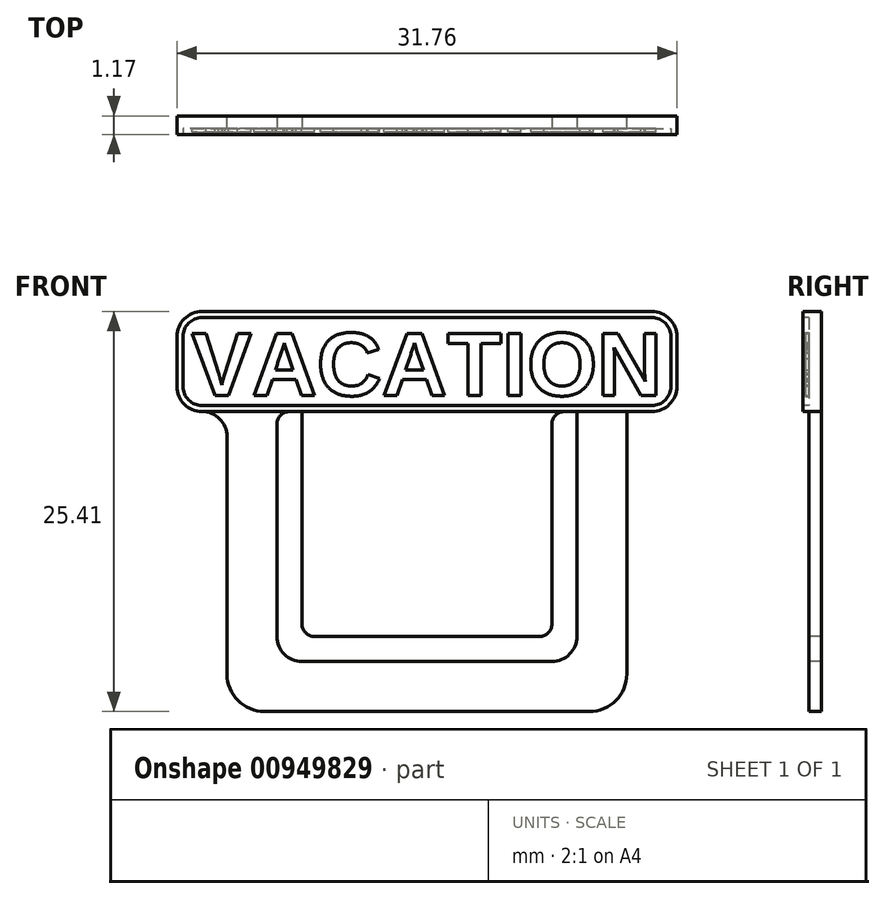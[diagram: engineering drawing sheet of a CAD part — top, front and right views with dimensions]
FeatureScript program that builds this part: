
annotation { "Feature Type Name" : "Feature", "Feature Type Description" : "" }
export const myFeature = defineFeature(function(context is Context, id is Id, definition is map)
    precondition{}
    {
        {
            var Q0;
            Q0=qCreatedBy(makeId("Front.planeOp"),FACE);
            var sketch = newSketch(context, id + "F0", { "sketchPlane" : qUnion([Q0])});
            skLineSegment(sketch, "E0.bottom", {"start": v(12.7, 9.53) * mm, "end": v(-12.7, 9.53) * mm});
            skLineSegment(sketch, "E0.top", {"start": v(12.7, -9.53) * mm, "end": v(-12.7, -9.53) * mm});
            skLineSegment(sketch, "E0.left", {"start": v(12.7, 9.53) * mm, "end": v(12.7, -9.53) * mm});
            skLineSegment(sketch, "E0.right", {"start": v(-12.7, 9.53) * mm, "end": v(-12.7, -9.53) * mm});
            skPoint(sketch, "E0.middle", {"position": v(0, 0) * mm});
            skSolve(sketch);
        }
        {
            var Q0;
            Q0=makeQuery(id+"F0.imprint","IMPRINT",FACE,{"disambiguationData":[TD([[makeQuery(id+"F0.imprint","IMPRINT",EDGE,{"derivedFrom":sQuery(id+"F0.wireOp",EDGE,"E0.bottom")}),1.0]])]});
            extrude(context, id + "F1", {"entities" : qUnion([Q0]), "depth" : 0.8 * mm, "offsetDistance" : 25.4 * mm});
        }
        {
            var Q0;
            Q0=makeQuery(id+"F1.opExtrude","SWEPT_EDGE",EDGE,{"disambiguationData":[OSD([sQuery(id+"F0.wireOp",EDGE,"E0.top"),sQuery(id+"F0.wireOp",EDGE,"E0.left")])]});
            var Q1;
            Q1=makeQuery(id+"F1.opExtrude","SWEPT_EDGE",EDGE,{"disambiguationData":[OSD([sQuery(id+"F0.wireOp",EDGE,"E0.top"),sQuery(id+"F0.wireOp",EDGE,"E0.right")])]});
            fillet(context, id + "F2", {"entities" : qUnion([Q0, Q1]), "radius" : 2.38 * mm, "tangentPropagation" : true, "allowEdgeOverflow" : false});
        }
        {
            var Q0;
            Q0=makeQuery(id+"F1.opExtrude","CAP_FACE",FACE,{"disambiguationData":[OSD([sQuery(id+"F0.wireOp",EDGE,"E0.bottom"),sQuery(id+"F0.wireOp",EDGE,"E0.top"),sQuery(id+"F0.wireOp",EDGE,"E0.left"),sQuery(id+"F0.wireOp",EDGE,"E0.right")])],"isStart":false});
            var sketch = newSketch(context, id + "F3", { "sketchPlane" : qUnion([Q0])});
            skLineSegment(sketch, "E1.bottom", {"start": v(9.52, 9.53) * mm, "end": v(-9.53, 9.53) * mm});
            skLineSegment(sketch, "E1.top", {"start": v(9.53, -6.35) * mm, "end": v(-9.53, -6.35) * mm});
            skLineSegment(sketch, "E1.left", {"start": v(9.52, 9.53) * mm, "end": v(9.53, -6.35) * mm});
            skLineSegment(sketch, "E1.right", {"start": v(-9.53, 9.53) * mm, "end": v(-9.52, -6.35) * mm});
            skPoint(sketch, "E1.middle", {"position": v(0, 0) * mm});
            skSolve(sketch);
        }
        {
            var Q0;
            Q0=makeQuery(id+"F3.imprint","IMPRINT",FACE,{"disambiguationData":[TD([[makeQuery(id+"F3.imprint","IMPRINT",EDGE,{"derivedFrom":sQuery(id+"F3.wireOp",EDGE,"E1.bottom")}),1.0]])]});
            extrude(context, id + "F4", {"entities" : qUnion([Q0]), "operationType" : NewBodyOperationType.REMOVE, "oppositeDirection" : true, "depth" : 4.93 * mm, "offsetDistance" : 25.4 * mm});
        }
        {
            var Q0;
            Q0=makeQuery(id+"F1.opExtrude","CAP_FACE",FACE,{"disambiguationData":[OSD([sQuery(id+"F0.wireOp",EDGE,"E0.bottom"),sQuery(id+"F0.wireOp",EDGE,"E0.top"),sQuery(id+"F0.wireOp",EDGE,"E0.left"),sQuery(id+"F0.wireOp",EDGE,"E0.right")])],"isStart":false});
            var sketch = newSketch(context, id + "F5", { "sketchPlane" : qUnion([Q0])});
            skLineSegment(sketch, "E2.bottom", {"start": v(-15.88, 9.53) * mm, "end": v(15.87, 9.53) * mm});
            skLineSegment(sketch, "E2.top", {"start": v(-15.88, 15.88) * mm, "end": v(15.87, 15.88) * mm});
            skLineSegment(sketch, "E2.left", {"start": v(-15.88, 9.53) * mm, "end": v(-15.88, 15.88) * mm});
            skLineSegment(sketch, "E2.right", {"start": v(15.87, 9.53) * mm, "end": v(15.87, 15.88) * mm});
            skSolve(sketch);
        }
        {
            var Q0;
            Q0=makeQuery(id+"F5.imprint","IMPRINT",FACE,{"disambiguationData":[TD([[makeQuery(id+"F5.imprint","IMPRINT",EDGE,{"derivedFrom":sQuery(id+"F5.wireOp",EDGE,"E2.top")}),-1.0]])]});
            extrude(context, id + "F6", {"entities" : qUnion([Q0]), "operationType" : NewBodyOperationType.ADD, "oppositeDirection" : true, "depth" : 0.8 * mm, "offsetDistance" : 25.4 * mm});
        }
        {
            var Q0;
            Q0=makeQuery(id+"F6.opExtrude","SWEPT_EDGE",EDGE,{"disambiguationData":[OSD([sQuery(id+"F5.wireOp",EDGE,"E2.top"),sQuery(id+"F5.wireOp",EDGE,"E2.left")])]});
            var Q1;
            Q1=makeQuery(id+"F6.opExtrude","SWEPT_EDGE",EDGE,{"disambiguationData":[OSD([sQuery(id+"F5.wireOp",EDGE,"E2.top"),sQuery(id+"F5.wireOp",EDGE,"E2.right")])]});
            var Q2;
            Q2=makeQuery(id+"F6.opExtrude","SWEPT_EDGE",EDGE,{"disambiguationData":[OSD([sQuery(id+"F5.wireOp",EDGE,"E2.bottom"),sQuery(id+"F5.wireOp",EDGE,"E2.right")])]});
            var Q3;
            Q3=makeQuery(id+"F1.opExtrude","SWEPT_EDGE",EDGE,{"disambiguationData":[OSD([sQuery(id+"F0.wireOp",EDGE,"E0.bottom"),sQuery(id+"F0.wireOp",EDGE,"E0.left")])]});
            var Q4;
            Q4=makeQuery(id+"F6.opExtrude","SWEPT_EDGE",EDGE,{"disambiguationData":[OSD([sQuery(id+"F5.wireOp",EDGE,"E2.bottom"),sQuery(id+"F5.wireOp",EDGE,"E2.left")])]});
            var Q5;
            Q5=makeQuery(id+"F1.opExtrude","SWEPT_EDGE",EDGE,{"disambiguationData":[OSD([sQuery(id+"F0.wireOp",EDGE,"E0.bottom"),sQuery(id+"F0.wireOp",EDGE,"E0.right")])]});
            fillet(context, id + "F7", {"entities" : qUnion([Q0, Q1, Q2, Q3, Q4, Q5]), "radius" : 1.59 * mm, "tangentPropagation" : true, "allowEdgeOverflow" : false});
        }
        {
            var Q0;
            Q0=makeQuery(id+"F4.boolean.opBoolean","COPY",EDGE,{"derivedFrom":makeQuery(id+"F4.opExtrude","SWEPT_EDGE",EDGE,{"disambiguationData":[OSD([sQuery(id+"F3.wireOp",EDGE,"E1.top"),sQuery(id+"F3.wireOp",EDGE,"E1.right")])]})});
            var Q1;
            Q1=makeQuery(id+"F4.boolean.opBoolean","COPY",EDGE,{"derivedFrom":makeQuery(id+"F4.opExtrude","SWEPT_EDGE",EDGE,{"disambiguationData":[OSD([sQuery(id+"F3.wireOp",EDGE,"E1.top"),sQuery(id+"F3.wireOp",EDGE,"E1.left")])]})});
            fillet(context, id + "F8", {"entities" : qUnion([Q0, Q1]), "radius" : 1.59 * mm, "tangentPropagation" : true, "allowEdgeOverflow" : false});
        }
        {
            var Q0;
            Q0=makeQuery(id+"F6.boolean.opBoolean","MERGE",FACE,{"derivedFrom":[makeQuery(id+"F1.opExtrude","CAP_FACE",FACE,{"disambiguationData":[OSD([sQuery(id+"F0.wireOp",EDGE,"E0.bottom"),sQuery(id+"F0.wireOp",EDGE,"E0.top"),sQuery(id+"F0.wireOp",EDGE,"E0.left"),sQuery(id+"F0.wireOp",EDGE,"E0.right")])],"isStart":false}),makeQuery(id+"F6.opExtrude","CAP_FACE",FACE,{"disambiguationData":[OSD([sQuery(id+"F5.wireOp",EDGE,"E2.bottom"),sQuery(id+"F5.wireOp",EDGE,"E2.top"),sQuery(id+"F5.wireOp",EDGE,"E2.left"),sQuery(id+"F5.wireOp",EDGE,"E2.right")])],"isStart":true})]});
            var sketch = newSketch(context, id + "F9", { "sketchPlane" : qUnion([Q0])});
            skLineSegment(sketch, "E3.bottom", {"start": v(-7.94, 9.53) * mm, "end": v(7.94, 9.53) * mm});
            skLineSegment(sketch, "E3.top", {"start": v(-7.94, -4.76) * mm, "end": v(7.94, -4.76) * mm});
            skLineSegment(sketch, "E3.left", {"start": v(-7.94, 9.53) * mm, "end": v(-7.94, -4.76) * mm});
            skLineSegment(sketch, "E3.right", {"start": v(7.94, 9.53) * mm, "end": v(7.94, -4.76) * mm});
            skSolve(sketch);
        }
        {
            var Q0;
            Q0=makeQuery(id+"F9.imprint","IMPRINT",FACE,{"disambiguationData":[TD([[makeQuery(id+"F9.imprint","IMPRINT",EDGE,{"derivedFrom":sQuery(id+"F9.wireOp",EDGE,"E3.bottom")}),1.0]])]});
            extrude(context, id + "F10", {"entities" : qUnion([Q0]), "operationType" : NewBodyOperationType.ADD, "oppositeDirection" : true, "depth" : 0.8 * mm, "offsetDistance" : 25.4 * mm});
        }
        {
            var Q0;
            Q0=makeQuery(id+"F10.opExtrude","SWEPT_EDGE",EDGE,{"disambiguationData":[OSD([sQuery(id+"F5.wireOp",EDGE,"E2.bottom"),sQuery(id+"F9.wireOp",EDGE,"E3.bottom"),sQuery(id+"F9.wireOp",EDGE,"E3.left")])]});
            var Q1;
            Q1=makeQuery(id+"F4.boolean.opBoolean","COPY",EDGE,{"derivedFrom":makeQuery(id+"F4.opExtrude","SWEPT_EDGE",EDGE,{"disambiguationData":[OSD([sQuery(id+"F0.wireOp",EDGE,"E0.bottom"),sQuery(id+"F3.wireOp",EDGE,"E1.bottom"),sQuery(id+"F3.wireOp",EDGE,"E1.right")])]})});
            var Q2;
            Q2=makeQuery(id+"F10.opExtrude","SWEPT_EDGE",EDGE,{"disambiguationData":[OSD([sQuery(id+"F5.wireOp",EDGE,"E2.bottom"),sQuery(id+"F9.wireOp",EDGE,"E3.bottom"),sQuery(id+"F9.wireOp",EDGE,"E3.right")])]});
            var Q3;
            Q3=makeQuery(id+"F4.boolean.opBoolean","COPY",EDGE,{"derivedFrom":makeQuery(id+"F4.opExtrude","SWEPT_EDGE",EDGE,{"disambiguationData":[OSD([sQuery(id+"F0.wireOp",EDGE,"E0.bottom"),sQuery(id+"F3.wireOp",EDGE,"E1.bottom"),sQuery(id+"F3.wireOp",EDGE,"E1.left")])]})});
            fillet(context, id + "F11", {"entities" : qUnion([Q0, Q1, Q2, Q3]), "radius" : 0.8 * mm, "tangentPropagation" : true, "allowEdgeOverflow" : false});
        }
        {
            var Q0;
            Q0=makeQuery(id+"F10.opExtrude","SWEPT_EDGE",EDGE,{"disambiguationData":[OSD([sQuery(id+"F9.wireOp",EDGE,"E3.top"),sQuery(id+"F9.wireOp",EDGE,"E3.left")])]});
            var Q1;
            Q1=makeQuery(id+"F10.opExtrude","SWEPT_EDGE",EDGE,{"disambiguationData":[OSD([sQuery(id+"F9.wireOp",EDGE,"E3.top"),sQuery(id+"F9.wireOp",EDGE,"E3.right")])]});
            fillet(context, id + "F12", {"entities" : qUnion([Q0, Q1]), "radius" : 0.8 * mm, "tangentPropagation" : true, "allowEdgeOverflow" : false});
        }
        {
            var Q0;
            Q0=makeQuery(id+"F10.boolean.opBoolean","MERGE",FACE,{"derivedFrom":[makeQuery(id+"F6.boolean.opBoolean","MERGE",FACE,{"derivedFrom":[makeQuery(id+"F1.opExtrude","CAP_FACE",FACE,{"disambiguationData":[OSD([sQuery(id+"F0.wireOp",EDGE,"E0.bottom"),sQuery(id+"F0.wireOp",EDGE,"E0.top"),sQuery(id+"F0.wireOp",EDGE,"E0.left"),sQuery(id+"F0.wireOp",EDGE,"E0.right")])],"isStart":false}),makeQuery(id+"F6.opExtrude","CAP_FACE",FACE,{"disambiguationData":[OSD([sQuery(id+"F5.wireOp",EDGE,"E2.bottom"),sQuery(id+"F5.wireOp",EDGE,"E2.top"),sQuery(id+"F5.wireOp",EDGE,"E2.left"),sQuery(id+"F5.wireOp",EDGE,"E2.right")])],"isStart":true})]}),makeQuery(id+"F10.opExtrude","CAP_FACE",FACE,{"disambiguationData":[OSD([sQuery(id+"F9.wireOp",EDGE,"E3.bottom"),sQuery(id+"F9.wireOp",EDGE,"E3.top"),sQuery(id+"F9.wireOp",EDGE,"E3.left"),sQuery(id+"F9.wireOp",EDGE,"E3.right")])],"isStart":true})]});
            var sketch = newSketch(context, id + "F13", { "sketchPlane" : qUnion([Q0])});
            skArc(sketch, "E4.0", {"start": v(-14.29, 15.88) * mm, "mid": v(-15.41, 15.41) * mm, "end": v(-15.88, 14.29) * mm});
            skLineSegment(sketch, "E5.0", {"start": v(-15.88, 11.11) * mm, "end": v(-15.88, 14.29) * mm});
            skArc(sketch, "E6.0", {"start": v(-15.88, 11.11) * mm, "mid": v(-15.41, 9.99) * mm, "end": v(-14.29, 9.53) * mm});
            skLineSegment(sketch, "E7.0", {"start": v(-14.29, 15.88) * mm, "end": v(14.29, 15.88) * mm});
            skArc(sketch, "E8.0", {"start": v(15.87, 14.29) * mm, "mid": v(15.41, 15.41) * mm, "end": v(14.29, 15.88) * mm});
            skLineSegment(sketch, "E9.0", {"start": v(15.87, 11.11) * mm, "end": v(15.87, 14.29) * mm});
            skArc(sketch, "E10.0", {"start": v(14.29, 9.53) * mm, "mid": v(15.41, 9.99) * mm, "end": v(15.87, 11.11) * mm});
            skLineSegment(sketch, "E11", {"start": v(-14.29, 9.53) * mm, "end": v(14.29, 9.53) * mm});
            skSolve(sketch);
        }
        {
            var Q0;
            Q0=makeQuery(id+"F13.imprint","IMPRINT",FACE,{"disambiguationData":[TD([[makeQuery(id+"F13.imprint","IMPRINT",EDGE,{"derivedFrom":sQuery(id+"F13.wireOp",EDGE,"E4.0")}),1.0]])]});
            extrude(context, id + "F14", {"entities" : qUnion([Q0]), "operationType" : NewBodyOperationType.ADD, "depth" : 0.38 * mm, "offsetDistance" : 25.4 * mm});
        }
        {
            var Q0;
            Q0=makeQuery(id+"F14.opExtrude","CAP_FACE",FACE,{"disambiguationData":[OSD([sQuery(id+"F13.wireOp",EDGE,"E4.0"),sQuery(id+"F13.wireOp",EDGE,"E5.0"),sQuery(id+"F13.wireOp",EDGE,"E6.0"),sQuery(id+"F13.wireOp",EDGE,"E7.0"),sQuery(id+"F13.wireOp",EDGE,"E8.0"),sQuery(id+"F13.wireOp",EDGE,"E9.0"),sQuery(id+"F13.wireOp",EDGE,"E10.0"),sQuery(id+"F13.wireOp",EDGE,"E11")])],"isStart":false});
            var sketch = newSketch(context, id + "F15", { "sketchPlane" : qUnion([Q0])});
            skArc(sketch, "E12.0", {"start": v(-14.29, 15.88) * mm, "mid": v(-15.41, 15.41) * mm, "end": v(-15.88, 14.29) * mm});
            skLineSegment(sketch, "E13.0", {"start": v(-14.29, 15.88) * mm, "end": v(14.29, 15.88) * mm});
            skLineSegment(sketch, "E14.0", {"start": v(-15.88, 11.11) * mm, "end": v(-15.88, 14.29) * mm});
            skArc(sketch, "E15.0", {"start": v(-15.88, 11.11) * mm, "mid": v(-15.41, 9.99) * mm, "end": v(-14.29, 9.53) * mm});
            skLineSegment(sketch, "E16.0", {"start": v(-14.29, 9.53) * mm, "end": v(14.29, 9.53) * mm});
            skArc(sketch, "E17.0", {"start": v(14.29, 9.53) * mm, "mid": v(15.41, 9.99) * mm, "end": v(15.87, 11.11) * mm});
            skArc(sketch, "E18.0", {"start": v(15.87, 14.29) * mm, "mid": v(15.41, 15.41) * mm, "end": v(14.29, 15.88) * mm});
            skArc(sketch, "E19", {"start": v(-14.29, 15.5) * mm, "mid": v(-15.14, 15.14) * mm, "end": v(-15.5, 14.29) * mm});
            skArc(sketch, "E20", {"start": v(-15.5, 11.11) * mm, "mid": v(-15.14, 10.26) * mm, "end": v(-14.29, 9.9) * mm});
            skArc(sketch, "E21", {"start": v(15.5, 14.29) * mm, "mid": v(15.14, 15.14) * mm, "end": v(14.29, 15.5) * mm});
            skArc(sketch, "E22", {"start": v(14.29, 9.9) * mm, "mid": v(15.14, 10.26) * mm, "end": v(15.5, 11.11) * mm});
            skLineSegment(sketch, "E23", {"start": v(-14.29, 15.88) * mm, "end": v(-14.29, 9.53) * mm, "construction": true});
            skLineSegment(sketch, "E24", {"start": v(-15.87, 14.29) * mm, "end": v(15.87, 14.29) * mm, "construction": true});
            skLineSegment(sketch, "E25", {"start": v(14.29, 15.88) * mm, "end": v(14.29, 9.53) * mm, "construction": true});
            skLineSegment(sketch, "E26", {"start": v(15.88, 11.11) * mm, "end": v(-15.88, 11.11) * mm, "construction": true});
            skLineSegment(sketch, "E27", {"start": v(14.29, 15.5) * mm, "end": v(-14.29, 15.5) * mm});
            skLineSegment(sketch, "E28", {"start": v(-15.5, 14.29) * mm, "end": v(-15.5, 11.11) * mm});
            skLineSegment(sketch, "E29", {"start": v(-14.29, 9.9) * mm, "end": v(14.29, 9.9) * mm});
            skLineSegment(sketch, "E30", {"start": v(15.5, 14.29) * mm, "end": v(15.5, 11.11) * mm});
            skSolve(sketch);
        }
        {
            var Q0;
            Q0=makeQuery(id+"F15.imprint","IMPRINT",FACE,{"disambiguationData":[TD([[makeQuery(id+"F15.imprint","IMPRINT",EDGE,{"derivedFrom":sQuery(id+"F15.wireOp",EDGE,"E19")}),1.0]])]});
            var Q1;
            {var subQ0=sQuery(id+"F9.wireOp",EDGE,"E3.right");var subQ1=sQuery(id+"F9.wireOp",EDGE,"E3.top");var subQ3=sQuery(id+"F0.wireOp",EDGE,"E0.bottom");var subQ4=sQuery(id+"F9.wireOp",EDGE,"E3.left");var subQ5=makeQuery(id+"F6.opExtrude","CAP_FACE",FACE,{"disambiguationData":[OSD([sQuery(id+"F5.wireOp",EDGE,"E2.bottom"),sQuery(id+"F5.wireOp",EDGE,"E2.top"),sQuery(id+"F5.wireOp",EDGE,"E2.left"),sQuery(id+"F5.wireOp",EDGE,"E2.right")])],"isStart":true});var subQ6=makeQuery(id+"F1.opExtrude","CAP_FACE",FACE,{"disambiguationData":[OSD([subQ3,sQuery(id+"F0.wireOp",EDGE,"E0.top"),sQuery(id+"F0.wireOp",EDGE,"E0.left"),sQuery(id+"F0.wireOp",EDGE,"E0.right")])],"isStart":false});var subQ7=makeQuery(id+"F10.opExtrude","CAP_FACE",FACE,{"disambiguationData":[OSD([sQuery(id+"F9.wireOp",EDGE,"E3.bottom"),subQ1,subQ4,subQ0])],"isStart":true});Q1=makeQuery(id+"F14.boolean.opBoolean","SPLIT",FACE,{"disambiguationData":[TD([makeQuery(id+"F10.opExtrude","SWEPT_FACE",FACE,{"disambiguationData":[OSD([subQ1])]})])],"derivedFrom":makeQuery(id+"F10.boolean.opBoolean","MERGE",FACE,{"derivedFrom":[makeQuery(id+"F6.boolean.opBoolean","MERGE",FACE,{"derivedFrom":[subQ6,subQ5]}),subQ7]})});}
            extrude(context, id + "F16", {"entities" : qUnion([Q0]), "operationType" : NewBodyOperationType.REMOVE, "endBound" : BoundingType.UP_TO_SURFACE, "oppositeDirection" : true, "depth" : 25.4 * mm, "endBoundEntityFace" : qUnion([Q1]), "offsetDistance" : 25.4 * mm});
        }
        {
            var Q0;
            Q0=qCreatedBy(makeId("Front.planeOp"),FACE);
            var sketch = newSketch(context, id + "F17", { "sketchPlane" : qUnion([Q0])});
            skText(sketch, "E31", { "text": "VACATION", "fontName": "Arimo-Bold.ttf"});
            const initialGuessF17  = {"E31": [-0.01494, 0.01055, 1, 0, 0.00412]};
            skSetInitialGuess(sketch, initialGuessF17);
            skSolve(sketch);
        }
        {
            var Q0;
            Q0=qSketchRegion(id+"F17",true);
            extrude(context, id + "F18", {"entities" : qUnion([Q0]), "operationType" : NewBodyOperationType.ADD, "depth" : 1.02 * mm, "offsetDistance" : 25.4 * mm});
        }
    });
